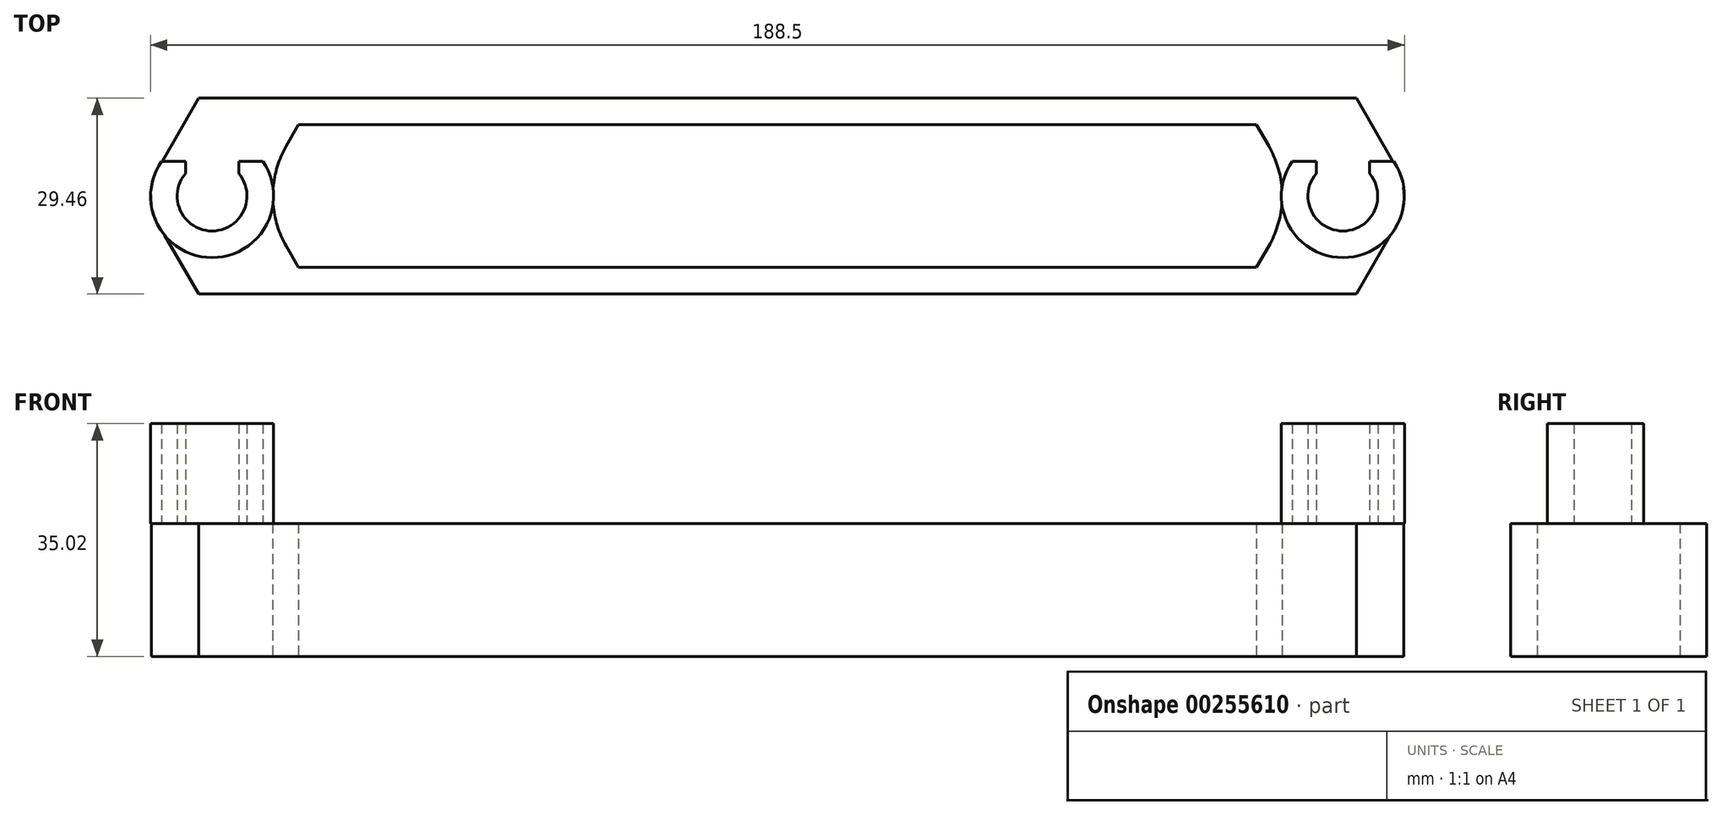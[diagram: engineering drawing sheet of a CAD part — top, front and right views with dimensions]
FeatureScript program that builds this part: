
annotation { "Feature Type Name" : "Feature", "Feature Type Description" : "" }
export const myFeature = defineFeature(function(context is Context, id is Id, definition is map)
    precondition{}
    {
        {
            var Q0;
            Q0=qCreatedBy(makeId("Top.planeOp"),FACE);
            var sketch = newSketch(context, id + "F0", { "sketchPlane" : qUnion([Q0])});
            skCircle(sketch, "E0", {"center": v(-85, 0) * mm, "radius": 5.12 * mm, "construction": true});
            skLineSegment(sketch, "E1.bottom", {"start": v(-87.03, 14.73) * mm, "end": v(87.03, 14.73) * mm});
            skLineSegment(sketch, "E1.top", {"start": v(-87.03, -14.73) * mm, "end": v(87.03, -14.73) * mm});
            skPoint(sketch, "E1.middle", {"position": v(0, 0) * mm});
            skLineSegment(sketch, "E2.bottom", {"start": v(-72, 10.73) * mm, "end": v(72, 10.73) * mm});
            skLineSegment(sketch, "E2.top", {"start": v(-72, -10.73) * mm, "end": v(72, -10.73) * mm});
            skCircle(sketch, "E3.MirrorC", {"center": v(85, 0) * mm, "radius": 5.12 * mm, "construction": true});
            skLineSegment(sketch, "E4", {"start": v(-87.03, 14.73) * mm, "end": v(-92.9, 4.56) * mm});
            skLineSegment(sketch, "E5", {"start": v(-92.9, -4.56) * mm, "end": v(-87.03, -14.73) * mm});
            skArc(sketch, "E6", {"start": v(-73.87, 7.5) * mm, "mid": v(-75.88, 0) * mm, "end": v(-73.87, -7.5) * mm});
            skLineSegment(sketch, "E7", {"start": v(-73.87, 7.5) * mm, "end": v(-72, 10.73) * mm});
            skLineSegment(sketch, "E8", {"start": v(-73.87, -7.5) * mm, "end": v(-72, -10.73) * mm});
            skLineSegment(sketch, "E9.MirrorCS", {"start": v(87.03, 14.73) * mm, "end": v(92.9, 4.56) * mm});
            skLineSegment(sketch, "E10.MirrorCS", {"start": v(73.87, 7.5) * mm, "end": v(72, 10.73) * mm});
            skArc(sketch, "E11.MirrorCS", {"start": v(73.87, 7.5) * mm, "mid": v(75.88, 0) * mm, "end": v(73.87, -7.5) * mm});
            skLineSegment(sketch, "E12.MirrorCS", {"start": v(73.87, -7.5) * mm, "end": v(72, -10.73) * mm});
            skLineSegment(sketch, "E13.MirrorCS", {"start": v(92.9, -4.56) * mm, "end": v(87.03, -14.73) * mm});
            skLineSegment(sketch, "E14", {"start": v(-92.9, 4.56) * mm, "end": v(-92.9, 4.56) * mm});
            skArc(sketch, "E15", {"start": v(-92.9, 4.56) * mm, "mid": v(-94.13, 0) * mm, "end": v(-92.9, -4.56) * mm});
            skArc(sketch, "E16", {"start": v(-92.9, -4.56) * mm, "mid": v(-75.88, 0) * mm, "end": v(-92.9, 4.56) * mm, "construction": true});
            skArc(sketch, "E17.MirrorCS", {"start": v(92.9, -4.56) * mm, "mid": v(75.88, 0) * mm, "end": v(92.9, 4.56) * mm, "construction": true});
            skArc(sketch, "E18.MirrorCS", {"start": v(92.9, 4.56) * mm, "mid": v(94.13, 0) * mm, "end": v(92.9, -4.56) * mm});
            skSolve(sketch);
        }
        {
            var Q0;
            Q0=makeQuery(id+"F0.imprint","IMPRINT",FACE,{"disambiguationData":[TD([[makeQuery(id+"F0.imprint","IMPRINT",EDGE,{"derivedFrom":sQuery(id+"F0.wireOp",EDGE,"E1.bottom")}),-1.0]])]});
            extrude(context, id + "F1", {"entities" : qUnion([Q0]), "depth" : 20.02 * mm});
        }
        {
            var Q0;
            Q0=makeQuery(id+"F1.opExtrude","CAP_FACE",FACE,{"disambiguationData":[OSD([sQuery(id+"F0.wireOp",EDGE,"E0"),sQuery(id+"F0.wireOp",EDGE,"E1.bottom"),sQuery(id+"F0.wireOp",EDGE,"E1.top"),sQuery(id+"F0.wireOp",EDGE,"E1.left"),sQuery(id+"F0.wireOp",EDGE,"E1.right"),sQuery(id+"F0.wireOp",EDGE,"E2.bottom"),sQuery(id+"F0.wireOp",EDGE,"E2.top"),sQuery(id+"F0.wireOp",EDGE,"E2.left"),sQuery(id+"F0.wireOp",EDGE,"E2.right"),sQuery(id+"F0.wireOp",EDGE,"E3.MirrorC")])],"isStart":false});
            var sketch = newSketch(context, id + "F2", { "sketchPlane" : qUnion([Q0])});
            skArc(sketch, "E19", {"start": v(-92.62, 5.25) * mm, "mid": v(-85, -9.25) * mm, "end": v(-77.38, 5.25) * mm});
            skLineSegment(sketch, "E20", {"start": v(-92.62, 5.25) * mm, "end": v(-89, 5.25) * mm});
            skLineSegment(sketch, "E21", {"start": v(-89, 5.25) * mm, "end": v(-89, 3.4) * mm});
            skLineSegment(sketch, "E22", {"start": v(-85, 0) * mm, "end": v(-85, 10.46) * mm, "construction": true});
            skLineSegment(sketch, "E23.MirrorCS", {"start": v(-81, 5.25) * mm, "end": v(-81, 3.4) * mm});
            skLineSegment(sketch, "E24.trimOffspring", {"start": v(-81, 5.25) * mm, "end": v(-77.38, 5.25) * mm});
            skArc(sketch, "E25.0", {"start": v(-89, 3.4) * mm, "mid": v(-85, -5.25) * mm, "end": v(-81, 3.4) * mm});
            skLineSegment(sketch, "E26.MirrorCS", {"start": v(81, 5.25) * mm, "end": v(81, 3.4) * mm});
            skLineSegment(sketch, "E27.MirrorCS", {"start": v(89, 5.25) * mm, "end": v(89, 3.4) * mm});
            skLineSegment(sketch, "E28.MirrorCS", {"start": v(81, 5.25) * mm, "end": v(77.38, 5.25) * mm});
            skArc(sketch, "E29.MirrorCS", {"start": v(89, 3.4) * mm, "mid": v(85, -5.25) * mm, "end": v(81, 3.4) * mm});
            skLineSegment(sketch, "E30.MirrorCS", {"start": v(85, 0) * mm, "end": v(85, 10.46) * mm, "construction": true});
            skLineSegment(sketch, "E31.MirrorCS", {"start": v(92.62, 5.25) * mm, "end": v(89, 5.25) * mm});
            skArc(sketch, "E32.MirrorCS", {"start": v(92.62, 5.25) * mm, "mid": v(85, -9.25) * mm, "end": v(77.38, 5.25) * mm});
            skSolve(sketch);
        }
        {
            var Q0;
            Q0 = qSketchRegion(id + "F2", true);
            extrude(context, id + "F3", {"entities" : qUnion([Q0]), "operationType" : NewBodyOperationType.ADD, "depth" : 15 * mm});
        }
    });
